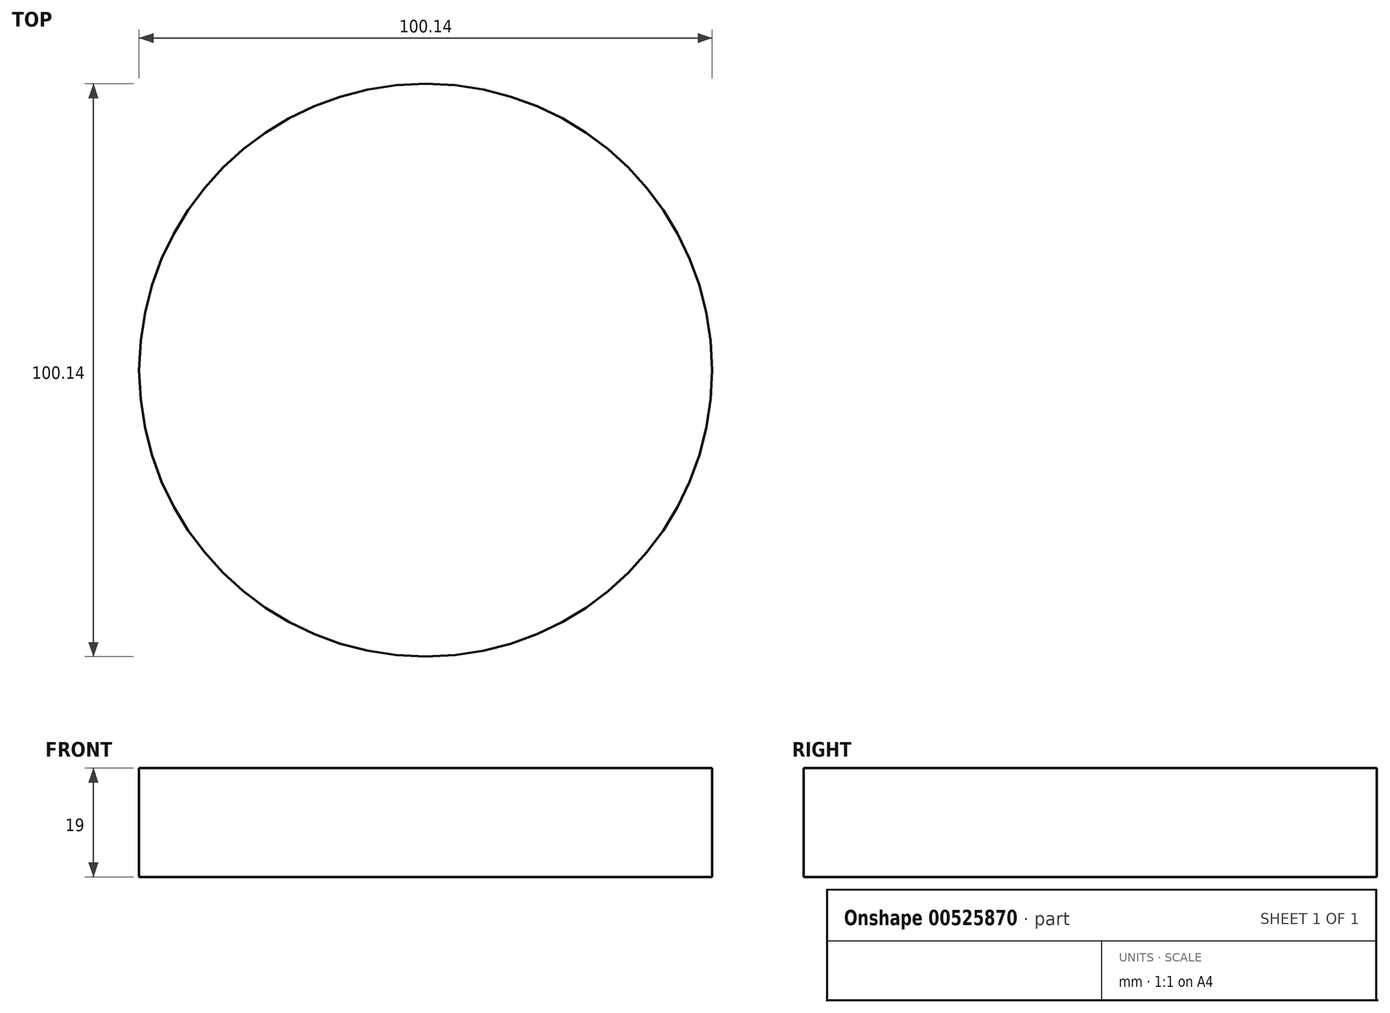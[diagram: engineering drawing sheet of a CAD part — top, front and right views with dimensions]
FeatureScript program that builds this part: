
annotation { "Feature Type Name" : "Feature", "Feature Type Description" : "" }
export const myFeature = defineFeature(function(context is Context, id is Id, definition is map)
    precondition{}
    {
        {
            var Q0;
            Q0=qCreatedBy(makeId("Top.planeOp"),FACE);
            var sketch = newSketch(context, id + "F0", { "sketchPlane" : qUnion([Q0])});
            skCircle(sketch, "E0", {"center": v(0, 0) * mm, "radius": 50.07 * mm});
            skSolve(sketch);
        }
        {
            var Q0;
            Q0=makeQuery(id+"F0.imprint","IMPRINT",FACE,{"disambiguationData":[TD([[makeQuery(id+"F0.imprint","IMPRINT",EDGE,{"derivedFrom":sQuery(id+"F0.wireOp",EDGE,"E0")}),1.0]])]});
            extrude(context, id + "F1", {"entities" : qUnion([Q0]), "depth" : 19 * mm, "offsetDistance" : 25 * mm});
        }
    });
